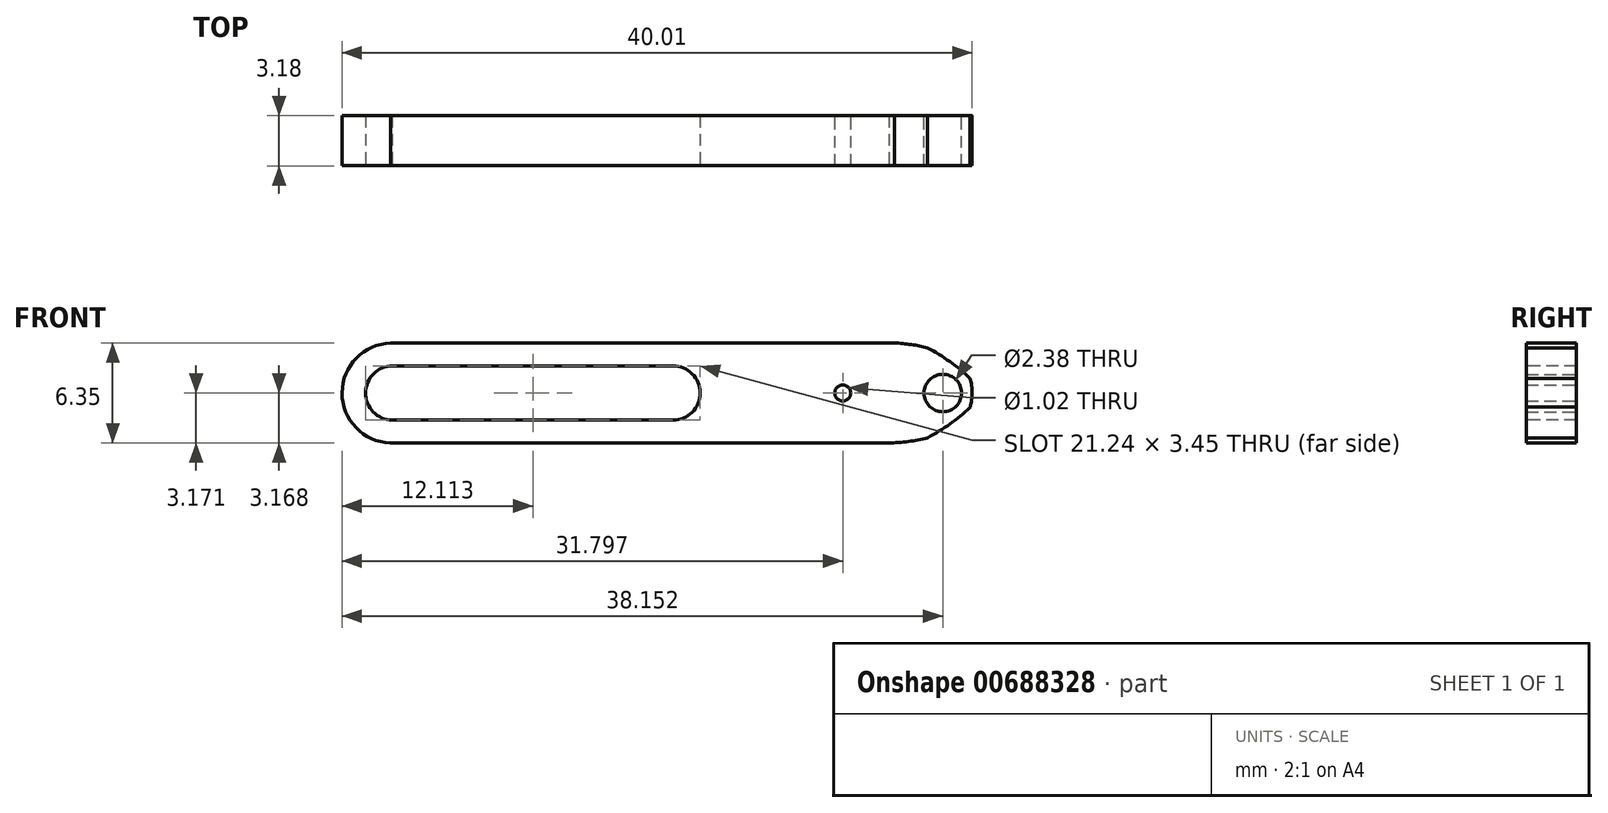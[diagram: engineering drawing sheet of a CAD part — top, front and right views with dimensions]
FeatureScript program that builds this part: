
annotation { "Feature Type Name" : "Feature", "Feature Type Description" : "" }
export const myFeature = defineFeature(function(context is Context, id is Id, definition is map)
    precondition{}
    {
        {
            var Q0;
            Q0=qCreatedBy(makeId("Front.planeOp"),FACE);
            var sketch = newSketch(context, id + "F0", { "sketchPlane" : qUnion([Q0])});
            skLineSegment(sketch, "E0", {"start": v(-12.91, 36.19) * mm, "end": v(-63.71, 36.19) * mm});
            skLineSegment(sketch, "E1", {"start": v(-63.71, 36.19) * mm, "end": v(-63.71, 42.54) * mm});
            skLineSegment(sketch, "E2", {"start": v(-12.91, 42.54) * mm, "end": v(-63.71, 42.54) * mm});
            skLineSegment(sketch, "E3", {"start": v(-12.91, 42.54) * mm, "end": v(-12.91, 36.19) * mm});
            skPoint(sketch, "E4", {"position": v(-17.35, 39.36) * mm});
            skPoint(sketch, "E4.positionSnap0", {"position": v(-12.91, 39.36) * mm});
            skCircle(sketch, "E5", {"center": v(-17.35, 39.36) * mm, "radius": 1.59 * mm});
            skLineSegment(sketch, "E6", {"start": v(-16.17, 42.54) * mm, "end": v(-12.91, 36.19) * mm});
            skLineSegment(sketch, "E7", {"start": v(-12.91, 42.54) * mm, "end": v(-16.17, 36.19) * mm});
            skArc(sketch, "E8", {"start": v(-59.99, 42.54) * mm, "mid": v(-63.07, 39.36) * mm, "end": v(-59.99, 36.19) * mm});
            skCircle(sketch, "E9", {"center": v(-17.35, 39.36) * mm, "radius": 1.2 * mm});
            skSolve(sketch);
        }
        {
            var Q0;
            Q0=makeQuery(id+"F0.imprint","IMPRINT",FACE,{"disambiguationData":[TD([[makeQuery(id+"F0.imprint","IMPRINT",EDGE,{"derivedFrom":sQuery(id+"F0.wireOp",EDGE,"E5")}),-1.0]])]});
            var Q1;
            Q1=makeQuery(id+"F0.imprint","IMPRINT",FACE,{"disambiguationData":[TD([[makeQuery(id+"F0.imprint","IMPRINT",EDGE,{"derivedFrom":sQuery(id+"F0.wireOp",EDGE,"E5")}),1.0]])]});
            extrude(context, id + "F1", {"entities" : qUnion([Q0, Q1]), "depth" : 3.17 * mm, "offsetDistance" : 25.4 * mm});
        }
        {
            var Q0;
            Q0=makeQuery(id+"F1.opExtrude","CAP_FACE",FACE,{"disambiguationData":[OSD([sQuery(id+"F0.wireOp",EDGE,"E0"),sQuery(id+"F0.wireOp",EDGE,"E2"),sQuery(id+"F0.wireOp",EDGE,"E5"),sQuery(id+"F0.wireOp",EDGE,"E6"),sQuery(id+"F0.wireOp",EDGE,"E7"),sQuery(id+"F0.wireOp",EDGE,"E8")])],"isStart":false});
            var sketch = newSketch(context, id + "F2", { "sketchPlane" : qUnion([Q0])});
            skArc(sketch, "E10", {"start": v(-17.33, 36.19) * mm, "mid": v(-14.97, 39.4) * mm, "end": v(-17.45, 42.54) * mm});
            skArc(sketch, "E11", {"start": v(-15.35, 40.95) * mm, "mid": v(-18.15, 42.19) * mm, "end": v(-21.2, 42.54) * mm});
            skArc(sketch, "E12", {"start": v(-21.18, 36.19) * mm, "mid": v(-18.15, 36.56) * mm, "end": v(-15.35, 37.77) * mm});
            skLineSegment(sketch, "E13", {"start": v(-59.9, 39.36) * mm, "end": v(-34.5, 39.36) * mm});
            skCircle(sketch, "E14", {"center": v(-34.5, 39.36) * mm, "radius": 1.73 * mm});
            skCircle(sketch, "E15", {"center": v(-59.9, 39.36) * mm, "radius": 1.73 * mm});
            skLineSegment(sketch, "E16", {"start": v(-59.9, 41.09) * mm, "end": v(-34.5, 41.09) * mm});
            skLineSegment(sketch, "E17", {"start": v(-34.5, 41.09) * mm, "end": v(-34.5, 37.63) * mm});
            skLineSegment(sketch, "E18", {"start": v(-34.5, 37.63) * mm, "end": v(-59.9, 37.63) * mm});
            skArc(sketch, "E19", {"start": v(-52.4, 42.54) * mm, "mid": v(-55.5, 39.38) * mm, "end": v(-52.44, 36.19) * mm});
            skArc(sketch, "E20", {"start": v(-52.3, 41.09) * mm, "mid": v(-54, 39.38) * mm, "end": v(-52.33, 37.63) * mm});
            skSolve(sketch);
        }
        {
            var Q0;
            {var subQ3=sQuery(id+"F2.wireOp",EDGE,"E10");Q0=makeQuery(id+"F2.imprint","IMPRINT",FACE,{"disambiguationData":[TD([[makeQuery(id+"F2.imprint","IMPRINT",EDGE,{"derivedFrom":subQ3}),-1.0]])]});}
            extrude(context, id + "F3", {"entities" : qUnion([Q0]), "operationType" : NewBodyOperationType.REMOVE, "oppositeDirection" : true, "depth" : 25.4 * mm, "offsetDistance" : 25.4 * mm});
        }
        {
            var Q0;
            {var subQ0=sQuery(id+"F2.wireOp",EDGE,"E10");var subQ1=makeQuery(id+"F1.opExtrude","CAP_EDGE",EDGE,{"disambiguationData":[OSD([sQuery(id+"F0.wireOp",EDGE,"E2")])],"isStart":false});var subQ2=makeQuery(id+"F2.imprint","INTERSECT",VERTEX,{"derivedFrom":[subQ1,subQ0]});Q0=makeQuery(id+"F2.imprint","IMPRINT",FACE,{"disambiguationData":[TD([[makeQuery(id+"F2.imprint","IMPRINT",EDGE,{"disambiguationData":[TD([[subQ2,1.0]])],"derivedFrom":subQ0}),1.0]])]});}
            var Q1;
            {var subQ5=sQuery(id+"F2.wireOp",EDGE,"E12");var subQ7=sQuery(id+"F2.wireOp",EDGE,"E10");var subQ8=makeQuery(id+"F2.imprint","INTERSECT",VERTEX,{"derivedFrom":[subQ7,subQ5]});Q1=makeQuery(id+"F2.imprint","IMPRINT",FACE,{"disambiguationData":[TD([[makeQuery(id+"F2.imprint","IMPRINT",EDGE,{"disambiguationData":[TD([[subQ8,-1.0]])],"derivedFrom":subQ7}),-1.0]])]});}
            var Q2;
            {var subQ0=sQuery(id+"F2.wireOp",EDGE,"E10");var subQ1=makeQuery(id+"F1.opExtrude","CAP_EDGE",EDGE,{"disambiguationData":[OSD([sQuery(id+"F0.wireOp",EDGE,"E0")])],"isStart":false});var subQ2=makeQuery(id+"F2.imprint","INTERSECT",VERTEX,{"derivedFrom":[subQ1,subQ0]});Q2=makeQuery(id+"F2.imprint","IMPRINT",FACE,{"disambiguationData":[TD([[makeQuery(id+"F2.imprint","IMPRINT",EDGE,{"disambiguationData":[TD([[subQ2,-1.0]])],"derivedFrom":subQ0}),1.0]])]});}
            extrude(context, id + "F4", {"entities" : qUnion([Q0, Q1, Q2]), "operationType" : NewBodyOperationType.REMOVE, "oppositeDirection" : true, "depth" : 25.4 * mm, "offsetDistance" : 25.4 * mm});
        }
        {
            var Q0;
            {var subQ10=makeQuery(id+"F1.opExtrude","CAP_EDGE",EDGE,{"disambiguationData":[OSD([sQuery(id+"F0.wireOp",EDGE,"E8")])],"isStart":false});Q0=makeQuery(id+"F2.imprint","IMPRINT",FACE,{"disambiguationData":[TD([[makeQuery(id+"F2.imprint","IMPRINT",EDGE,{"derivedFrom":subQ10}),1.0]])]});}
            var Q1;
            {var subQ0=sQuery(id+"F2.wireOp",EDGE,"E15");var subQ1=sQuery(id+"F2.wireOp",EDGE,"E13");var subQ2=makeQuery(id+"F2.imprint","INTERSECT",VERTEX,{"derivedFrom":[subQ1,subQ0]});Q1=makeQuery(id+"F2.imprint","IMPRINT",FACE,{"disambiguationData":[TD([[makeQuery(id+"F2.imprint","IMPRINT",EDGE,{"disambiguationData":[TD([[subQ2,-1.0]])],"derivedFrom":subQ1}),1.0]])]});}
            var Q2;
            {var subQ0=sQuery(id+"F2.wireOp",EDGE,"E15");var subQ1=sQuery(id+"F2.wireOp",EDGE,"E13");var subQ2=makeQuery(id+"F2.imprint","INTERSECT",VERTEX,{"derivedFrom":[subQ1,subQ0]});Q2=makeQuery(id+"F2.imprint","IMPRINT",FACE,{"disambiguationData":[TD([[makeQuery(id+"F2.imprint","IMPRINT",EDGE,{"disambiguationData":[TD([[subQ2,-1.0]])],"derivedFrom":subQ1}),-1.0]])]});}
            var Q3;
            {var subQ0=sQuery(id+"F2.wireOp",EDGE,"E15");var subQ1=makeQuery(id+"F2.imprint","INTERSECT",VERTEX,{"derivedFrom":[subQ0,sQuery(id+"F2.wireOp",EDGE,"E16")]});Q3=makeQuery(id+"F2.imprint","IMPRINT",FACE,{"disambiguationData":[TD([[makeQuery(id+"F2.imprint","IMPRINT",EDGE,{"disambiguationData":[TD([[subQ1,1.0]])],"derivedFrom":subQ0}),1.0]])]});}
            extrude(context, id + "F5", {"entities" : qUnion([Q0, Q1, Q2, Q3]), "operationType" : NewBodyOperationType.REMOVE, "oppositeDirection" : true, "depth" : 25.4 * mm, "offsetDistance" : 25.4 * mm});
        }
        {
            var Q0;
            {var subQ0=sQuery(id+"F2.wireOp",EDGE,"E20");var subQ1=sQuery(id+"F2.wireOp",EDGE,"E13");var subQ2=makeQuery(id+"F2.imprint","INTERSECT",VERTEX,{"derivedFrom":[subQ1,subQ0]});Q0=makeQuery(id+"F2.imprint","IMPRINT",FACE,{"disambiguationData":[TD([[makeQuery(id+"F2.imprint","IMPRINT",EDGE,{"disambiguationData":[TD([[subQ2,-1.0]])],"derivedFrom":subQ1}),1.0]])]});}
            var Q1;
            {var subQ0=sQuery(id+"F2.wireOp",EDGE,"E20");var subQ1=sQuery(id+"F2.wireOp",EDGE,"E13");var subQ2=makeQuery(id+"F2.imprint","INTERSECT",VERTEX,{"derivedFrom":[subQ1,subQ0]});Q1=makeQuery(id+"F2.imprint","IMPRINT",FACE,{"disambiguationData":[TD([[makeQuery(id+"F2.imprint","IMPRINT",EDGE,{"disambiguationData":[TD([[subQ2,-1.0]])],"derivedFrom":subQ1}),-1.0]])]});}
            var Q2;
            {var subQ0=sQuery(id+"F2.wireOp",EDGE,"E17");var subQ1=sQuery(id+"F2.wireOp",EDGE,"E13");var subQ2=makeQuery(id+"F2.imprint","INTERSECT",VERTEX,{"derivedFrom":[subQ1,subQ0]});Q2=makeQuery(id+"F2.imprint","IMPRINT",FACE,{"disambiguationData":[TD([[makeQuery(id+"F2.imprint","IMPRINT",EDGE,{"disambiguationData":[TD([[subQ2,1.0]])],"derivedFrom":subQ1}),1.0]])]});}
            var Q3;
            {var subQ0=sQuery(id+"F2.wireOp",EDGE,"E17");var subQ1=sQuery(id+"F2.wireOp",EDGE,"E13");var subQ2=makeQuery(id+"F2.imprint","INTERSECT",VERTEX,{"derivedFrom":[subQ1,subQ0]});Q3=makeQuery(id+"F2.imprint","IMPRINT",FACE,{"disambiguationData":[TD([[makeQuery(id+"F2.imprint","IMPRINT",EDGE,{"disambiguationData":[TD([[subQ2,1.0]])],"derivedFrom":subQ1}),-1.0]])]});}
            var Q4;
            {var subQ0=sQuery(id+"F2.wireOp",EDGE,"E17");var subQ4=makeQuery(id+"F2.imprint","INTERSECT",VERTEX,{"derivedFrom":[sQuery(id+"F2.wireOp",EDGE,"E13"),subQ0]});Q4=makeQuery(id+"F2.imprint","IMPRINT",FACE,{"disambiguationData":[TD([[makeQuery(id+"F2.imprint","IMPRINT",EDGE,{"disambiguationData":[TD([[subQ4,1.0]])],"derivedFrom":subQ0}),1.0]])]});}
            extrude(context, id + "F6", {"entities" : qUnion([Q0, Q1, Q2, Q3, Q4]), "operationType" : NewBodyOperationType.REMOVE, "oppositeDirection" : true, "depth" : 25.4 * mm, "offsetDistance" : 25.4 * mm});
        }
        {
            var Q0;
            Q0=makeQuery(id+"F2.imprint","IMPRINT",FACE,{"disambiguationData":[TD([[makeQuery(id+"F2.imprint","IMPRINT",EDGE,{"derivedFrom":makeQuery(id+"F1.opExtrude","CAP_EDGE",EDGE,{"disambiguationData":[OSD([sQuery(id+"F0.wireOp",EDGE,"E9")])],"isStart":false})}),-1.0]])]});
            var sketch = newSketch(context, id + "F7", { "sketchPlane" : qUnion([Q0])});
            skArc(sketch, "E21", {"start": v(-17.3, 36.21) * mm, "mid": v(-15.5, 39.43) * mm, "end": v(-17.43, 42.57) * mm});
            skArc(sketch, "E22", {"start": v(-12.85, 36.5) * mm, "mid": v(-15.57, 40.25) * mm, "end": v(-19.46, 42.78) * mm});
            skArc(sketch, "E23", {"start": v(-19.52, 35.96) * mm, "mid": v(-15.58, 38.49) * mm, "end": v(-12.85, 42.3) * mm});
            skSolve(sketch);
        }
        {
            var Q0;
            {var subQ2=sQuery(id+"F2.wireOp",EDGE,"E10");var subQ6=sQuery(id+"F2.wireOp",EDGE,"E12");var subQ7=makeQuery(id+"F2.imprint","INTERSECT",VERTEX,{"derivedFrom":[subQ2,subQ6]});var subQ10=makeQuery(id+"F2.imprint","IMPRINT",EDGE,{"disambiguationData":[TD([[subQ7,-1.0]])],"derivedFrom":subQ2});Q0=makeQuery(id+"F7.imprint","IMPRINT",FACE,{"disambiguationData":[TD([[makeQuery(id+"F7.imprint","IMPRINT",EDGE,{"derivedFrom":subQ10}),1.0]])]});}
            extrude(context, id + "F8", {"entities" : qUnion([Q0]), "operationType" : NewBodyOperationType.REMOVE, "oppositeDirection" : true, "depth" : 25.4 * mm, "offsetDistance" : 25.4 * mm});
        }
        {
            var Q0;
            {var subQ0=sQuery(id+"F7.wireOp",EDGE,"E22");var subQ1=sQuery(id+"F7.wireOp",EDGE,"E21");var subQ2=makeQuery(id+"F7.imprint","INTERSECT",VERTEX,{"derivedFrom":[subQ1,subQ0]});Q0=makeQuery(id+"F7.imprint","IMPRINT",FACE,{"disambiguationData":[TD([[makeQuery(id+"F7.imprint","IMPRINT",EDGE,{"disambiguationData":[TD([[subQ2,-1.0]])],"derivedFrom":subQ1}),1.0]])]});}
            var Q1;
            {var subQ0=sQuery(id+"F7.wireOp",EDGE,"E23");var subQ1=sQuery(id+"F7.wireOp",EDGE,"E21");var subQ2=makeQuery(id+"F7.imprint","INTERSECT",VERTEX,{"derivedFrom":[subQ1,subQ0]});Q1=makeQuery(id+"F7.imprint","IMPRINT",FACE,{"disambiguationData":[TD([[makeQuery(id+"F7.imprint","IMPRINT",EDGE,{"disambiguationData":[TD([[subQ2,1.0]])],"derivedFrom":subQ1}),1.0]])]});}
            extrude(context, id + "F9", {"entities" : qUnion([Q0, Q1]), "operationType" : NewBodyOperationType.REMOVE, "oppositeDirection" : true, "depth" : 21.59 * mm, "offsetDistance" : 25.4 * mm});
        }
        {
            var Q0;
            Q0=makeQuery(id+"F0.imprint","IMPRINT",FACE,{"disambiguationData":[TD([[makeQuery(id+"F0.imprint","IMPRINT",EDGE,{"derivedFrom":sQuery(id+"F0.wireOp",EDGE,"E5")}),-1.0]])]});
            var sketch = newSketch(context, id + "F10", { "sketchPlane" : qUnion([Q0])});
            skLineSegment(sketch, "E24", {"start": v(-17.35, 39.36) * mm, "end": v(-23.7, 39.36) * mm});
            skPoint(sketch, "E25", {"position": v(-23.7, 39.36) * mm});
            skSolve(sketch);
        }
        {
            var Q0;
            Q0=sQuery(id+"F10.wireOp",VERTEX,"E24.end");
            var Q1;
            Q1=makeQuery(id+"F1.opExtrude","SWEPT_BODY",BODY,{"disambiguationData":[OSD([sQuery(id+"F0.wireOp",EDGE,"E0"),sQuery(id+"F0.wireOp",EDGE,"E2"),sQuery(id+"F0.wireOp",EDGE,"E6"),sQuery(id+"F0.wireOp",EDGE,"E7"),sQuery(id+"F0.wireOp",EDGE,"E8"),sQuery(id+"F0.wireOp",EDGE,"E9")])]});
            hole(context, id + "F11", {"style" : HoleStyle.SIMPLE, "endStyle" : HoleEndStyle.THROUGH, "oppositeDirection" : true, "holeDiameter" : 1.02 * mm, "majorDiameter" : 6.35 * mm, "isTappedThrough" : true, "tappedDepth" : 12.7 * mm, "tapClearance" : 3, "locations" : qUnion([Q0]), "scope" : qUnion([Q1])});
        }
    });
